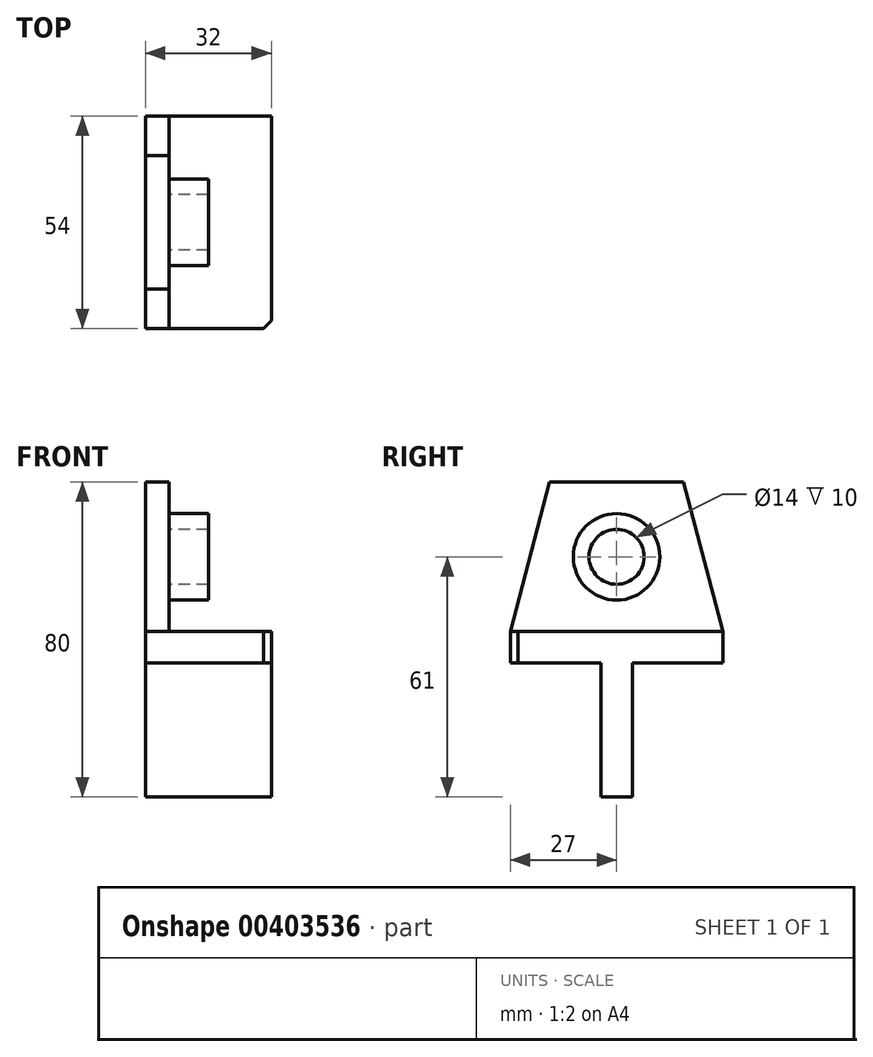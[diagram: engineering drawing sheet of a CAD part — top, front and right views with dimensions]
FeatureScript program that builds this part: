
annotation { "Feature Type Name" : "Feature", "Feature Type Description" : "" }
export const myFeature = defineFeature(function(context is Context, id is Id, definition is map)
    precondition{}
    {
        {
            var Q0;
            Q0=qCreatedBy(makeId("Right.planeOp"),FACE);
            var sketch = newSketch(context, id + "F0", { "sketchPlane" : qUnion([Q0])});
            skLineSegment(sketch, "E0", {"start": v(-27, 0) * mm, "end": v(27, 0) * mm});
            skLineSegment(sketch, "E1", {"start": v(27, 0) * mm, "end": v(27, -8) * mm});
            skLineSegment(sketch, "E2", {"start": v(27, -8) * mm, "end": v(4, -8) * mm});
            skLineSegment(sketch, "E3", {"start": v(4, -8) * mm, "end": v(4, -42) * mm});
            skLineSegment(sketch, "E4", {"start": v(4, -42) * mm, "end": v(-4, -42) * mm});
            skLineSegment(sketch, "E5", {"start": v(-4, -42) * mm, "end": v(-4, -8) * mm});
            skLineSegment(sketch, "E6", {"start": v(-4, -8) * mm, "end": v(-27, -8) * mm});
            skLineSegment(sketch, "E7", {"start": v(-27, -8) * mm, "end": v(-27, 0) * mm});
            skSolve(sketch);
        }
        {
            var Q0;
            Q0 = qSketchRegion(id + "F0", true);
            extrude(context, id + "F1", {"entities" : qUnion([Q0]), "oppositeDirection" : true, "depth" : 32 * mm});
        }
        {
            var Q0;
            Q0=makeQuery(id+"F1.opExtrude","CAP_FACE",FACE,{"disambiguationData":[OSD([sQuery(id+"F0.wireOp",EDGE,"E0"),sQuery(id+"F0.wireOp",EDGE,"E1"),sQuery(id+"F0.wireOp",EDGE,"E2"),sQuery(id+"F0.wireOp",EDGE,"E3"),sQuery(id+"F0.wireOp",EDGE,"E4"),sQuery(id+"F0.wireOp",EDGE,"E5"),sQuery(id+"F0.wireOp",EDGE,"E6"),sQuery(id+"F0.wireOp",EDGE,"E7")])],"isStart":false});
            var sketch = newSketch(context, id + "F2", { "sketchPlane" : qUnion([Q0])});
            skLineSegment(sketch, "E8", {"start": v(27, 0) * mm, "end": v(17, 38) * mm});
            skLineSegment(sketch, "E9", {"start": v(17, 38) * mm, "end": v(-17, 38) * mm});
            skLineSegment(sketch, "E10", {"start": v(-17, 38) * mm, "end": v(-27, 0) * mm});
            skLineSegment(sketch, "E11", {"start": v(27, 0) * mm, "end": v(-27, 0) * mm});
            skSolve(sketch);
        }
        {
            var Q0;
            Q0 = qSketchRegion(id + "F2", true);
            extrude(context, id + "F3", {"entities" : qUnion([Q0]), "operationType" : NewBodyOperationType.ADD, "oppositeDirection" : true, "depth" : 6 * mm});
        }
        {
            var Q0;
            Q0=makeQuery(id+"F3.opExtrude","CAP_FACE",FACE,{"disambiguationData":[OSD([sQuery(id+"F2.wireOp",EDGE,"E8"),sQuery(id+"F2.wireOp",EDGE,"E9"),sQuery(id+"F2.wireOp",EDGE,"E10"),sQuery(id+"F2.wireOp",EDGE,"E11")])],"isStart":false});
            var sketch = newSketch(context, id + "F4", { "sketchPlane" : qUnion([Q0])});
            skCircle(sketch, "E12", {"center": v(0, 19) * mm, "radius": 11 * mm});
            skCircle(sketch, "E13", {"center": v(0, 19) * mm, "radius": 7 * mm});
            skSolve(sketch);
        }
        {
            var Q0;
            Q0 = qSketchRegion(id + "F4", true);
            extrude(context, id + "F5", {"entities" : qUnion([Q0]), "operationType" : NewBodyOperationType.ADD, "depth" : 10 * mm});
        }
        {
            var Q0;
            Q0=makeQuery(id+"F1.opExtrude","CAP_EDGE",EDGE,{"disambiguationData":[OSD([sQuery(id+"F0.wireOp",EDGE,"E7")])],"isStart":true});
            chamfer(context, id + "F6", {"entities" : qUnion([Q0]), "width" : 2 * mm, "tangentPropagation" : true});
        }
    });
